# Revit family: VUTR 200 V(E)K(S) EC
name_source: partatom
category: Mechanical Equipment
units: mm (PartAtom-declared; Revit-internal decimal feet)

## family parameters
Always vertical = Yes
Cut with Voids When Loaded = No
OmniClass Number = 23.75.00.00
OmniClass Title = Climate Control (HVAC)
Part Type = Normal
Room Calculation Point = No
Round Connector Dimension = Use Diameter
Shared = No
Work Plane-Based = No

## types (2) — shared parameters
00_20_Manufacturer = Vents
00_20_Name = Single-room air handling unit with heat recovery
D = 125 mm  [stored 0.410105 ft]
Filter = G4
Frequency = 60 Hz
H = 792 mm  [stored 2.59843 ft]
L = 338 mm  [stored 1.10892 ft]
Load Classification = HVAC
Maintenance zone material = <By Category>
Maximum Air Flow = 270.0 m³/h
Number of Fase = 1
Sound pressure level at 3 m distance = 33 dBA
Voltage = 230 V
W = 599 mm  [stored 1.96522 ft]
zero-valued in all types: Default Elevation

## per-type parameters (varying)
| type | Amperage | Casing Material | Power | Weight |
| VUTR 200 VK(S) ЕС | 1 A | Сталь | 171 W | 51.60 kg |
| VUTR 200 VEK(S) EC | 4 A | Polypropylene (white) | 871 W | 52.60 kg |

note: column(s) folded — value = type name in every type: 00_20_Type

note: [stored X ft] marks values corroborated as IEEE doubles in the binary element streams (Revit-internal decimal feet)

## geometry (parser evidence)
native form markers: Sweep x13
no freeform markers — native parametric forms only
